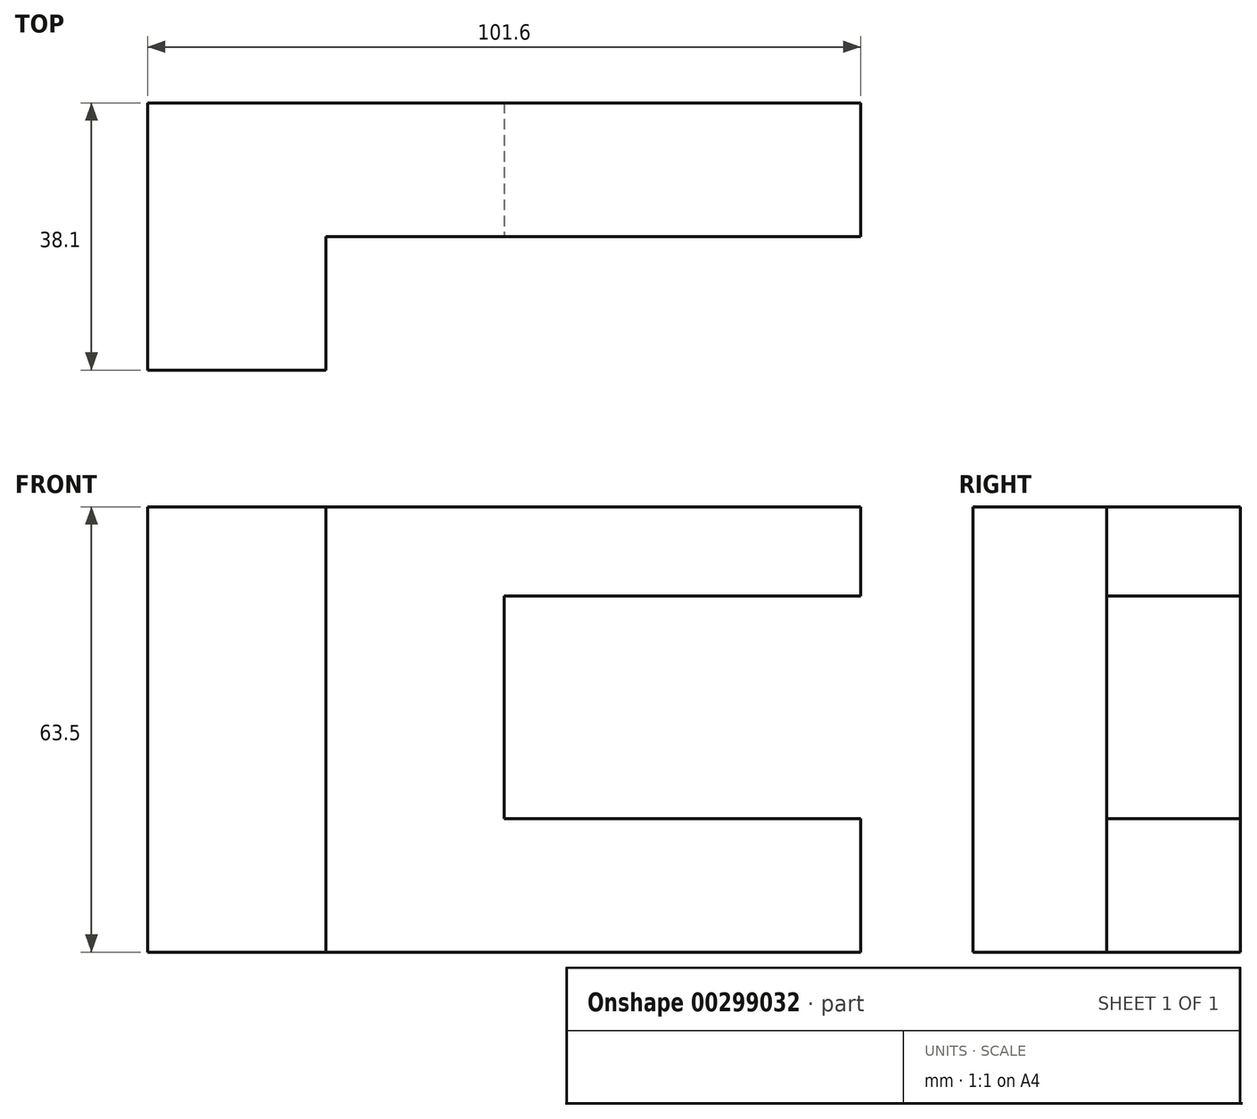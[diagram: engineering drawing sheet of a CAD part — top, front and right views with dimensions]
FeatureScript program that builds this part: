
annotation { "Feature Type Name" : "Feature", "Feature Type Description" : "" }
export const myFeature = defineFeature(function(context is Context, id is Id, definition is map)
    precondition{}
    {
        {
            var Q0;
            Q0=qCreatedBy(makeId("Front.planeOp"),FACE);
            var sketch = newSketch(context, id + "F0", { "sketchPlane" : qUnion([Q0])});
            skLineSegment(sketch, "E0.bottom", {"start": v(-50.8, 31.75) * mm, "end": v(50.8, 31.75) * mm});
            skLineSegment(sketch, "E0.top", {"start": v(-50.8, -31.75) * mm, "end": v(50.8, -31.75) * mm});
            skLineSegment(sketch, "E0.left", {"start": v(-50.8, 31.75) * mm, "end": v(-50.8, -31.75) * mm});
            skLineSegment(sketch, "E0.right", {"start": v(50.8, 31.75) * mm, "end": v(50.8, -31.75) * mm});
            skPoint(sketch, "E0.middle", {"position": v(0, 0) * mm});
            skSolve(sketch);
        }
        {
            var Q0;
            Q0=makeQuery(id+"F0.imprint","IMPRINT",FACE,{"disambiguationData":[TD([[makeQuery(id+"F0.imprint","IMPRINT",EDGE,{"derivedFrom":sQuery(id+"F0.wireOp",EDGE,"E0.bottom")}),-1.0]])]});
            extrude(context, id + "F1", {"entities" : qUnion([Q0]), "depth" : 19.05 * mm});
        }
        {
            var Q0;
            Q0=makeQuery(id+"F1.opExtrude","CAP_FACE",FACE,{"disambiguationData":[OSD([sQuery(id+"F0.wireOp",EDGE,"E0.bottom"),sQuery(id+"F0.wireOp",EDGE,"E0.top"),sQuery(id+"F0.wireOp",EDGE,"E0.left"),sQuery(id+"F0.wireOp",EDGE,"E0.right")])],"isStart":false});
            var sketch = newSketch(context, id + "F2", { "sketchPlane" : qUnion([Q0])});
            skLineSegment(sketch, "E1.bottom", {"start": v(50.8, -12.7) * mm, "end": v(0, -12.7) * mm});
            skLineSegment(sketch, "E1.top", {"start": v(50.8, 19.05) * mm, "end": v(0, 19.05) * mm});
            skLineSegment(sketch, "E1.left", {"start": v(50.8, -12.7) * mm, "end": v(50.8, 19.05) * mm});
            skLineSegment(sketch, "E1.right", {"start": v(0, -12.7) * mm, "end": v(0, 19.05) * mm});
            skSolve(sketch);
        }
        {
            var Q0;
            Q0=makeQuery(id+"F2.imprint","IMPRINT",FACE,{"disambiguationData":[TD([[makeQuery(id+"F2.imprint","IMPRINT",EDGE,{"derivedFrom":sQuery(id+"F2.wireOp",EDGE,"E1.bottom")}),-1.0]])]});
            extrude(context, id + "F3", {"entities" : qUnion([Q0]), "operationType" : NewBodyOperationType.REMOVE, "endBound" : BoundingType.THROUGH_ALL, "oppositeDirection" : true, "depth" : 25.4 * mm});
        }
        {
            var Q0;
            Q0=makeQuery(id+"F1.opExtrude","CAP_FACE",FACE,{"disambiguationData":[OSD([sQuery(id+"F0.wireOp",EDGE,"E0.bottom"),sQuery(id+"F0.wireOp",EDGE,"E0.top"),sQuery(id+"F0.wireOp",EDGE,"E0.left"),sQuery(id+"F0.wireOp",EDGE,"E0.right")])],"isStart":false});
            var sketch = newSketch(context, id + "F4", { "sketchPlane" : qUnion([Q0])});
            skLineSegment(sketch, "E2.bottom", {"start": v(-50.8, -31.75) * mm, "end": v(-25.4, -31.75) * mm});
            skLineSegment(sketch, "E2.top", {"start": v(-50.8, 31.75) * mm, "end": v(-25.4, 31.75) * mm});
            skLineSegment(sketch, "E2.left", {"start": v(-50.8, -31.75) * mm, "end": v(-50.8, 31.75) * mm});
            skLineSegment(sketch, "E2.right", {"start": v(-25.4, -31.75) * mm, "end": v(-25.4, 31.75) * mm});
            skSolve(sketch);
        }
        {
            var Q0;
            Q0=makeQuery(id+"F4.imprint","IMPRINT",FACE,{"disambiguationData":[TD([[makeQuery(id+"F4.imprint","IMPRINT",EDGE,{"derivedFrom":sQuery(id+"F4.wireOp",EDGE,"E2.bottom")}),1.0]])]});
            extrude(context, id + "F5", {"entities" : qUnion([Q0]), "operationType" : NewBodyOperationType.ADD, "depth" : 19.05 * mm});
        }
    });
